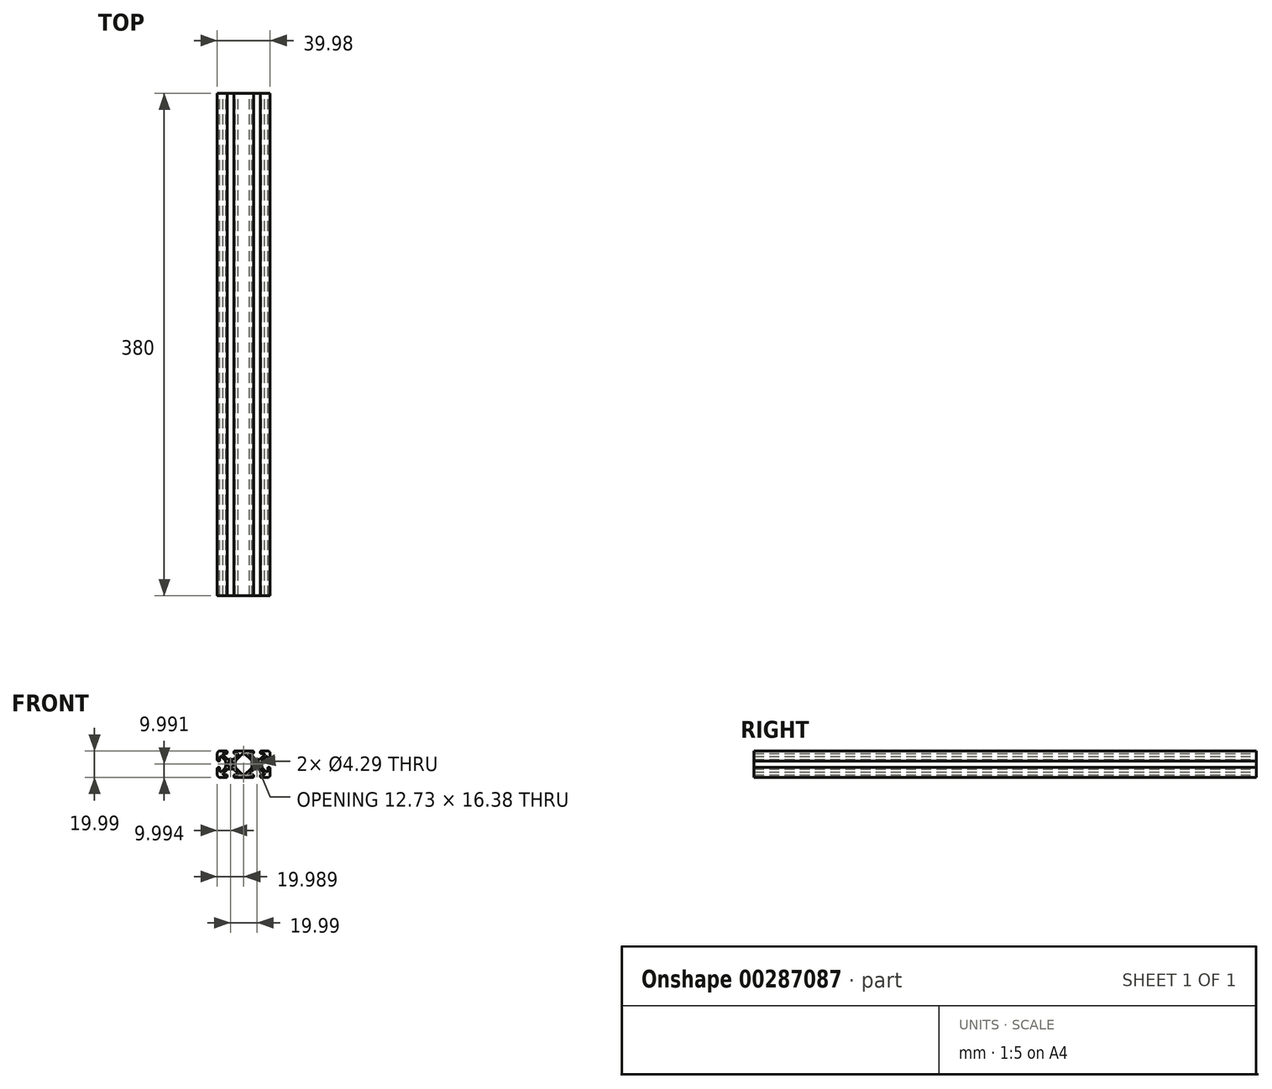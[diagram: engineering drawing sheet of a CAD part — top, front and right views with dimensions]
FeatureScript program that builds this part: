
annotation { "Feature Type Name" : "Feature", "Feature Type Description" : "" }
export const myFeature = defineFeature(function(context is Context, id is Id, definition is map)
    precondition{}
    {
        {
            var Q0;
            Q0=qCreatedBy(makeId("Front.planeOp"),FACE);
            var sketch = newSketch(context, id + "F0", { "sketchPlane" : qUnion([Q0])});
            skArc(sketch, "E0.0.0", {"start": v(-12.02, 4.76) * mm, "mid": v(-13.17, 4.99) * mm, "end": v(-14.14, 5.64) * mm});
            skLineSegment(sketch, "E0.0.1", {"start": v(-14.14, 5.64) * mm, "end": v(-16.4, 7.9) * mm});
            skArc(sketch, "E0.0.2", {"start": v(-16.4, 7.9) * mm, "mid": v(-16.58, 8.8) * mm, "end": v(-15.8, 9.32) * mm});
            skLineSegment(sketch, "E0.0.3", {"start": v(-15.8, 9.32) * mm, "end": v(-13.7, 9.32) * mm});
            skArc(sketch, "E0.0.4", {"start": v(-13.7, 9.32) * mm, "mid": v(-13.48, 9.41) * mm, "end": v(-13.39, 9.63) * mm});
            skLineSegment(sketch, "E0.0.5", {"start": v(-13.39, 9.63) * mm, "end": v(-13.39, 10.34) * mm});
            skArc(sketch, "E0.0.6", {"start": v(-13.39, 10.34) * mm, "mid": v(-13.62, 10.9) * mm, "end": v(-14.18, 11.13) * mm});
            skLineSegment(sketch, "E0.0.7", {"start": v(-14.18, 11.13) * mm, "end": v(-18.87, 11.13) * mm});
            skArc(sketch, "E0.0.8", {"start": v(-18.87, 11.13) * mm, "mid": v(-20.3, 10.54) * mm, "end": v(-20.88, 9.12) * mm});
            skLineSegment(sketch, "E0.0.9", {"start": v(-20.88, 9.12) * mm, "end": v(-20.88, 4.42) * mm});
            skArc(sketch, "E0.0.10", {"start": v(-20.88, 4.42) * mm, "mid": v(-20.65, 3.86) * mm, "end": v(-20.1, 3.63) * mm});
            skLineSegment(sketch, "E0.0.11", {"start": v(-20.1, 3.63) * mm, "end": v(-19.38, 3.63) * mm});
            skArc(sketch, "E0.0.12", {"start": v(-19.38, 3.63) * mm, "mid": v(-19.17, 3.72) * mm, "end": v(-19.08, 3.94) * mm});
            skLineSegment(sketch, "E0.0.13", {"start": v(-19.08, 3.94) * mm, "end": v(-19.08, 6.05) * mm});
            skArc(sketch, "E0.0.14", {"start": v(-19.08, 6.05) * mm, "mid": v(-18.56, 6.82) * mm, "end": v(-17.65, 6.64) * mm});
            skLineSegment(sketch, "E0.0.15", {"start": v(-17.65, 6.64) * mm, "end": v(-15.4, 4.38) * mm});
            skArc(sketch, "E0.0.16", {"start": v(-15.4, 4.38) * mm, "mid": v(-14.74, 3.41) * mm, "end": v(-14.51, 2.26) * mm});
            skLineSegment(sketch, "E0.0.17", {"start": v(-14.51, 2.26) * mm, "end": v(-14.51, 0) * mm});
            skArc(sketch, "E0.0.18", {"start": v(-14.51, 0) * mm, "mid": v(-14.74, -1.15) * mm, "end": v(-15.4, -2.12) * mm});
            skLineSegment(sketch, "E0.0.19", {"start": v(-15.4, -2.12) * mm, "end": v(-17.65, -4.38) * mm});
            skArc(sketch, "E0.0.20", {"start": v(-17.65, -4.38) * mm, "mid": v(-18.56, -4.56) * mm, "end": v(-19.08, -3.78) * mm});
            skLineSegment(sketch, "E0.0.21", {"start": v(-19.08, -3.78) * mm, "end": v(-19.08, -1.68) * mm});
            skArc(sketch, "E0.0.22", {"start": v(-19.08, -1.68) * mm, "mid": v(-19.17, -1.46) * mm, "end": v(-19.38, -1.37) * mm});
            skLineSegment(sketch, "E0.0.23", {"start": v(-19.38, -1.37) * mm, "end": v(-20.1, -1.37) * mm});
            skArc(sketch, "E0.0.24", {"start": v(-20.1, -1.37) * mm, "mid": v(-20.65, -1.6) * mm, "end": v(-20.88, -2.16) * mm});
            skLineSegment(sketch, "E0.0.25", {"start": v(-20.88, -2.16) * mm, "end": v(-20.88, -6.86) * mm});
            skArc(sketch, "E0.0.26", {"start": v(-20.88, -6.86) * mm, "mid": v(-20.3, -8.28) * mm, "end": v(-18.87, -8.86) * mm});
            skLineSegment(sketch, "E0.0.27", {"start": v(-18.87, -8.86) * mm, "end": v(-14.18, -8.86) * mm});
            skArc(sketch, "E0.0.28", {"start": v(-14.18, -8.86) * mm, "mid": v(-13.62, -8.63) * mm, "end": v(-13.39, -8.08) * mm});
            skLineSegment(sketch, "E0.0.29", {"start": v(-13.39, -8.08) * mm, "end": v(-13.39, -7.36) * mm});
            skArc(sketch, "E0.0.30", {"start": v(-13.39, -7.36) * mm, "mid": v(-13.48, -7.15) * mm, "end": v(-13.7, -7.06) * mm});
            skLineSegment(sketch, "E0.0.31", {"start": v(-13.7, -7.06) * mm, "end": v(-15.8, -7.06) * mm});
            skArc(sketch, "E0.0.32", {"start": v(-15.8, -7.06) * mm, "mid": v(-16.58, -6.54) * mm, "end": v(-16.4, -5.63) * mm});
            skLineSegment(sketch, "E0.0.33", {"start": v(-16.4, -5.63) * mm, "end": v(-14.14, -3.37) * mm});
            skArc(sketch, "E0.0.34", {"start": v(-14.14, -3.37) * mm, "mid": v(-13.17, -2.72) * mm, "end": v(-12.02, -2.5) * mm});
            skLineSegment(sketch, "E0.0.35", {"start": v(-12.02, -2.5) * mm, "end": v(-9.75, -2.5) * mm});
            skArc(sketch, "E0.0.36", {"start": v(-9.75, -2.5) * mm, "mid": v(-8.6, -2.72) * mm, "end": v(-7.63, -3.37) * mm});
            skLineSegment(sketch, "E0.0.37", {"start": v(-7.63, -3.37) * mm, "end": v(-5.38, -5.63) * mm});
            skArc(sketch, "E0.0.38", {"start": v(-5.38, -5.63) * mm, "mid": v(-5.2, -6.54) * mm, "end": v(-5.97, -7.06) * mm});
            skLineSegment(sketch, "E0.0.39", {"start": v(-5.97, -7.06) * mm, "end": v(-8.08, -7.06) * mm});
            skArc(sketch, "E0.0.40", {"start": v(-8.08, -7.06) * mm, "mid": v(-8.3, -7.15) * mm, "end": v(-8.38, -7.36) * mm});
            skLineSegment(sketch, "E0.0.41", {"start": v(-8.38, -7.36) * mm, "end": v(-8.38, -8.08) * mm});
            skArc(sketch, "E0.0.42", {"start": v(-8.38, -8.08) * mm, "mid": v(-8.15, -8.63) * mm, "end": v(-7.6, -8.86) * mm});
            skLineSegment(sketch, "E0.0.43", {"start": v(-7.6, -8.86) * mm, "end": v(5.81, -8.86) * mm});
            skArc(sketch, "E0.0.44", {"start": v(5.81, -8.86) * mm, "mid": v(6.37, -8.63) * mm, "end": v(6.6, -8.08) * mm});
            skLineSegment(sketch, "E0.0.45", {"start": v(6.6, -8.08) * mm, "end": v(6.6, -7.36) * mm});
            skArc(sketch, "E0.0.46", {"start": v(6.6, -7.36) * mm, "mid": v(6.51, -7.15) * mm, "end": v(6.3, -7.06) * mm});
            skLineSegment(sketch, "E0.0.47", {"start": v(6.3, -7.06) * mm, "end": v(4.19, -7.06) * mm});
            skArc(sketch, "E0.0.48", {"start": v(4.19, -7.06) * mm, "mid": v(3.41, -6.54) * mm, "end": v(3.6, -5.63) * mm});
            skLineSegment(sketch, "E0.0.49", {"start": v(3.6, -5.63) * mm, "end": v(5.85, -3.37) * mm});
            skArc(sketch, "E0.0.50", {"start": v(5.85, -3.37) * mm, "mid": v(6.82, -2.72) * mm, "end": v(7.97, -2.5) * mm});
            skLineSegment(sketch, "E0.0.51", {"start": v(7.97, -2.5) * mm, "end": v(10.24, -2.5) * mm});
            skArc(sketch, "E0.0.52", {"start": v(10.24, -2.5) * mm, "mid": v(11.38, -2.72) * mm, "end": v(12.36, -3.37) * mm});
            skLineSegment(sketch, "E0.0.53", {"start": v(12.36, -3.37) * mm, "end": v(14.61, -5.63) * mm});
            skArc(sketch, "E0.0.54", {"start": v(14.61, -5.63) * mm, "mid": v(14.8, -6.54) * mm, "end": v(14.02, -7.06) * mm});
            skLineSegment(sketch, "E0.0.55", {"start": v(14.02, -7.06) * mm, "end": v(11.91, -7.06) * mm});
            skArc(sketch, "E0.0.56", {"start": v(11.91, -7.06) * mm, "mid": v(11.7, -7.15) * mm, "end": v(11.6, -7.36) * mm});
            skLineSegment(sketch, "E0.0.57", {"start": v(11.6, -7.36) * mm, "end": v(11.6, -8.08) * mm});
            skArc(sketch, "E0.0.58", {"start": v(11.6, -8.08) * mm, "mid": v(11.84, -8.63) * mm, "end": v(12.4, -8.86) * mm});
            skLineSegment(sketch, "E0.0.59", {"start": v(12.4, -8.86) * mm, "end": v(17.1, -8.86) * mm});
            skArc(sketch, "E0.0.60", {"start": v(17.1, -8.86) * mm, "mid": v(18.51, -8.28) * mm, "end": v(19.1, -6.86) * mm});
            skLineSegment(sketch, "E0.0.61", {"start": v(19.1, -6.86) * mm, "end": v(19.1, -2.16) * mm});
            skArc(sketch, "E0.0.62", {"start": v(19.1, -2.16) * mm, "mid": v(18.87, -1.6) * mm, "end": v(18.31, -1.37) * mm});
            skLineSegment(sketch, "E0.0.63", {"start": v(18.31, -1.37) * mm, "end": v(17.6, -1.37) * mm});
            skArc(sketch, "E0.0.64", {"start": v(17.6, -1.37) * mm, "mid": v(17.38, -1.46) * mm, "end": v(17.3, -1.68) * mm});
            skLineSegment(sketch, "E0.0.65", {"start": v(17.3, -1.68) * mm, "end": v(17.3, -3.78) * mm});
            skArc(sketch, "E0.0.66", {"start": v(17.3, -3.78) * mm, "mid": v(16.78, -4.56) * mm, "end": v(15.86, -4.38) * mm});
            skLineSegment(sketch, "E0.0.67", {"start": v(15.86, -4.38) * mm, "end": v(13.6, -2.12) * mm});
            skArc(sketch, "E0.0.68", {"start": v(13.6, -2.12) * mm, "mid": v(12.96, -1.15) * mm, "end": v(12.73, 0) * mm});
            skLineSegment(sketch, "E0.0.69", {"start": v(12.73, 0) * mm, "end": v(12.73, 2.26) * mm});
            skArc(sketch, "E0.0.70", {"start": v(12.73, 2.26) * mm, "mid": v(12.96, 3.41) * mm, "end": v(13.6, 4.38) * mm});
            skLineSegment(sketch, "E0.0.71", {"start": v(13.6, 4.38) * mm, "end": v(15.86, 6.64) * mm});
            skArc(sketch, "E0.0.72", {"start": v(15.86, 6.64) * mm, "mid": v(16.78, 6.82) * mm, "end": v(17.3, 6.05) * mm});
            skLineSegment(sketch, "E0.0.73", {"start": v(17.3, 6.05) * mm, "end": v(17.3, 3.94) * mm});
            skArc(sketch, "E0.0.74", {"start": v(17.3, 3.94) * mm, "mid": v(17.38, 3.72) * mm, "end": v(17.6, 3.63) * mm});
            skLineSegment(sketch, "E0.0.75", {"start": v(17.6, 3.63) * mm, "end": v(18.31, 3.63) * mm});
            skArc(sketch, "E0.0.76", {"start": v(18.31, 3.63) * mm, "mid": v(18.87, 3.86) * mm, "end": v(19.1, 4.42) * mm});
            skLineSegment(sketch, "E0.0.77", {"start": v(19.1, 4.42) * mm, "end": v(19.1, 9.12) * mm});
            skArc(sketch, "E0.0.78", {"start": v(19.1, 9.12) * mm, "mid": v(18.51, 10.54) * mm, "end": v(17.1, 11.13) * mm});
            skLineSegment(sketch, "E0.0.79", {"start": v(17.1, 11.13) * mm, "end": v(12.4, 11.13) * mm});
            skArc(sketch, "E0.0.80", {"start": v(12.4, 11.13) * mm, "mid": v(11.84, 10.9) * mm, "end": v(11.6, 10.34) * mm});
            skLineSegment(sketch, "E0.0.81", {"start": v(11.6, 10.34) * mm, "end": v(11.6, 9.63) * mm});
            skArc(sketch, "E0.0.82", {"start": v(11.6, 9.63) * mm, "mid": v(11.7, 9.41) * mm, "end": v(11.91, 9.32) * mm});
            skLineSegment(sketch, "E0.0.83", {"start": v(11.91, 9.32) * mm, "end": v(14.02, 9.32) * mm});
            skArc(sketch, "E0.0.84", {"start": v(14.02, 9.32) * mm, "mid": v(14.8, 8.8) * mm, "end": v(14.61, 7.9) * mm});
            skLineSegment(sketch, "E0.0.85", {"start": v(14.61, 7.9) * mm, "end": v(12.36, 5.64) * mm});
            skArc(sketch, "E0.0.86", {"start": v(12.36, 5.64) * mm, "mid": v(11.38, 4.99) * mm, "end": v(10.24, 4.76) * mm});
            skLineSegment(sketch, "E0.0.87", {"start": v(10.24, 4.76) * mm, "end": v(7.97, 4.76) * mm});
            skArc(sketch, "E0.0.88", {"start": v(7.97, 4.76) * mm, "mid": v(6.82, 4.99) * mm, "end": v(5.85, 5.64) * mm});
            skLineSegment(sketch, "E0.0.89", {"start": v(5.85, 5.64) * mm, "end": v(3.6, 7.9) * mm});
            skArc(sketch, "E0.0.90", {"start": v(3.6, 7.9) * mm, "mid": v(3.41, 8.8) * mm, "end": v(4.19, 9.32) * mm});
            skLineSegment(sketch, "E0.0.91", {"start": v(4.19, 9.32) * mm, "end": v(6.3, 9.32) * mm});
            skArc(sketch, "E0.0.92", {"start": v(6.3, 9.32) * mm, "mid": v(6.51, 9.41) * mm, "end": v(6.6, 9.63) * mm});
            skLineSegment(sketch, "E0.0.93", {"start": v(6.6, 9.63) * mm, "end": v(6.6, 10.34) * mm});
            skArc(sketch, "E0.0.94", {"start": v(6.6, 10.34) * mm, "mid": v(6.37, 10.9) * mm, "end": v(5.81, 11.13) * mm});
            skLineSegment(sketch, "E0.0.95", {"start": v(5.81, 11.13) * mm, "end": v(-7.6, 11.13) * mm});
            skArc(sketch, "E0.0.96", {"start": v(-7.6, 11.13) * mm, "mid": v(-8.15, 10.9) * mm, "end": v(-8.38, 10.34) * mm});
            skLineSegment(sketch, "E0.0.97", {"start": v(-8.38, 10.34) * mm, "end": v(-8.38, 9.63) * mm});
            skArc(sketch, "E0.0.98", {"start": v(-8.38, 9.63) * mm, "mid": v(-8.3, 9.41) * mm, "end": v(-8.08, 9.32) * mm});
            skLineSegment(sketch, "E0.0.99", {"start": v(-8.08, 9.32) * mm, "end": v(-5.97, 9.32) * mm});
            skArc(sketch, "E0.0.100", {"start": v(-5.97, 9.32) * mm, "mid": v(-5.2, 8.8) * mm, "end": v(-5.38, 7.9) * mm});
            skLineSegment(sketch, "E0.0.101", {"start": v(-5.38, 7.9) * mm, "end": v(-7.63, 5.64) * mm});
            skArc(sketch, "E0.0.102", {"start": v(-7.63, 5.64) * mm, "mid": v(-8.6, 4.99) * mm, "end": v(-9.75, 4.76) * mm});
            skLineSegment(sketch, "E0.0.103", {"start": v(-9.75, 4.76) * mm, "end": v(-12.02, 4.76) * mm});
            skCircle(sketch, "E1.0", {"center": v(-10.89, 1.13) * mm, "radius": 2.15 * mm});
            skCircle(sketch, "E2.0", {"center": v(9.1, 1.13) * mm, "radius": 2.15 * mm});
            skLineSegment(sketch, "E3.0", {"start": v(-7.26, 2.26) * mm, "end": v(-7.26, 0) * mm});
            skArc(sketch, "E3.1", {"start": v(-6.38, 4.38) * mm, "mid": v(-7.03, 3.41) * mm, "end": v(-7.26, 2.26) * mm});
            skLineSegment(sketch, "E3.2", {"start": v(-1.83, 8.93) * mm, "end": v(-6.38, 4.38) * mm});
            skArc(sketch, "E3.3", {"start": v(-7.26, 0) * mm, "mid": v(-7.03, -1.15) * mm, "end": v(-6.38, -2.12) * mm});
            skLineSegment(sketch, "E3.4", {"start": v(-6.38, -2.12) * mm, "end": v(-1.83, -6.67) * mm});
            skArc(sketch, "E3.5", {"start": v(-1.83, -6.67) * mm, "mid": v(-0.9, -7.06) * mm, "end": v(0.05, -6.67) * mm});
            skLineSegment(sketch, "E3.6", {"start": v(0.05, -6.67) * mm, "end": v(4.6, -2.12) * mm});
            skLineSegment(sketch, "E3.7", {"start": v(4.6, 4.38) * mm, "end": v(0.05, 8.93) * mm});
            skLineSegment(sketch, "E3.8", {"start": v(5.48, 0) * mm, "end": v(5.48, 2.26) * mm});
            skArc(sketch, "E3.9", {"start": v(5.48, 2.26) * mm, "mid": v(5.25, 3.41) * mm, "end": v(4.6, 4.38) * mm});
            skArc(sketch, "E3.10", {"start": v(4.6, -2.12) * mm, "mid": v(5.25, -1.15) * mm, "end": v(5.48, 0) * mm});
            skArc(sketch, "E3.11", {"start": v(0.05, 8.93) * mm, "mid": v(-0.9, 9.32) * mm, "end": v(-1.83, 8.93) * mm});
            skSolve(sketch);
        }
        {
            var Q0;
            Q0=qSketchRegion(id+"F0",true);
            extrude(context, id + "F1", {"entities" : qUnion([Q0]), "depth" : 380 * mm});
        }
    });
